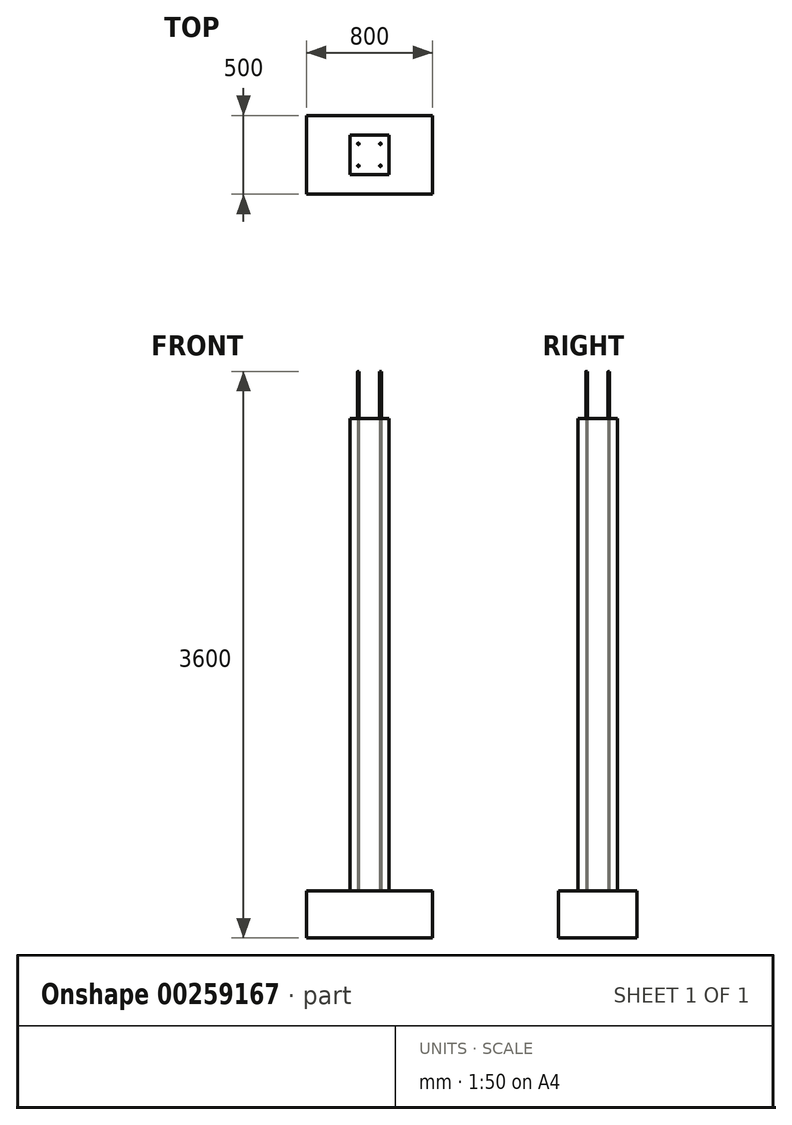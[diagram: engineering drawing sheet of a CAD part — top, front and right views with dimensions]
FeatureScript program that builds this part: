
annotation { "Feature Type Name" : "Feature", "Feature Type Description" : "" }
export const myFeature = defineFeature(function(context is Context, id is Id, definition is map)
    precondition{}
    {
        {
            var Q0;
            Q0=qCreatedBy(makeId("Top.planeOp"),FACE);
            var sketch = newSketch(context, id + "F0", { "sketchPlane" : qUnion([Q0])});
            skLineSegment(sketch, "E0.bottom", {"start": v(125, 125) * mm, "end": v(-125, 125) * mm});
            skLineSegment(sketch, "E0.top", {"start": v(125, -125) * mm, "end": v(-125, -125) * mm});
            skLineSegment(sketch, "E0.left", {"start": v(125, 125) * mm, "end": v(125, -125) * mm});
            skLineSegment(sketch, "E0.right", {"start": v(-125, 125) * mm, "end": v(-125, -125) * mm});
            skPoint(sketch, "E0.middle", {"position": v(0, 0) * mm});
            skSolve(sketch);
        }
        {
            var Q0;
            Q0 = qSketchRegion(id + "F0", true);
            extrude(context, id + "F1", {"entities" : qUnion([Q0]), "depth" : 3000 * mm});
        }
        {
            var Q0;
            Q0=qCreatedBy(makeId("Top.planeOp"),FACE);
            var sketch = newSketch(context, id + "F2", { "sketchPlane" : qUnion([Q0])});
            skLineSegment(sketch, "E1.bottom", {"start": v(-125, -125) * mm, "end": v(125, -125) * mm, "construction": true});
            skLineSegment(sketch, "E1.top", {"start": v(-125, 125) * mm, "end": v(125, 125) * mm, "construction": true});
            skLineSegment(sketch, "E1.left", {"start": v(-125, -125) * mm, "end": v(-125, 125) * mm, "construction": true});
            skLineSegment(sketch, "E1.right", {"start": v(125, -125) * mm, "end": v(125, 125) * mm, "construction": true});
            skPoint(sketch, "E1.middle", {"position": v(0, 0) * mm});
            skLineSegment(sketch, "E2.bottom", {"start": v(-70, -70) * mm, "end": v(70, -70) * mm, "construction": true});
            skLineSegment(sketch, "E2.top", {"start": v(-70, 70) * mm, "end": v(70, 70) * mm, "construction": true});
            skLineSegment(sketch, "E2.left", {"start": v(-70, -70) * mm, "end": v(-70, 70) * mm, "construction": true});
            skLineSegment(sketch, "E2.right", {"start": v(70, -70) * mm, "end": v(70, 70) * mm, "construction": true});
            skCircle(sketch, "E3", {"center": v(70, -70) * mm, "radius": 5 * mm});
            skCircle(sketch, "E4", {"center": v(70, 70) * mm, "radius": 5 * mm});
            skCircle(sketch, "E5", {"center": v(-70, 70) * mm, "radius": 5 * mm});
            skCircle(sketch, "E6", {"center": v(-70, -70) * mm, "radius": 5 * mm});
            skCircle(sketch, "E7", {"center": v(0, 0) * mm, "radius": 125 * mm, "construction": true});
            skSolve(sketch);
        }
        {
            var Q0;
            Q0 = qSketchRegion(id + "F2", true);
            extrude(context, id + "F3", {"entities" : qUnion([Q0]), "depth" : 3300 * mm});
        }
        {
            var Q0;
            Q0=qCreatedBy(makeId("Top.planeOp"),FACE);
            var sketch = newSketch(context, id + "F4", { "sketchPlane" : qUnion([Q0])});
            skLineSegment(sketch, "E8.bottom", {"start": v(400, 250) * mm, "end": v(-400, 250) * mm});
            skLineSegment(sketch, "E8.top", {"start": v(400, -250) * mm, "end": v(-400, -250) * mm});
            skLineSegment(sketch, "E8.left", {"start": v(400, 250) * mm, "end": v(400, -250) * mm});
            skLineSegment(sketch, "E8.right", {"start": v(-400, 250) * mm, "end": v(-400, -250) * mm});
            skPoint(sketch, "E8.middle", {"position": v(0, 0) * mm});
            skSolve(sketch);
        }
        {
            var Q0;
            Q0 = qSketchRegion(id + "F4", true);
            extrude(context, id + "F5", {"entities" : qUnion([Q0]), "oppositeDirection" : true, "depth" : 300 * mm});
        }
    });
